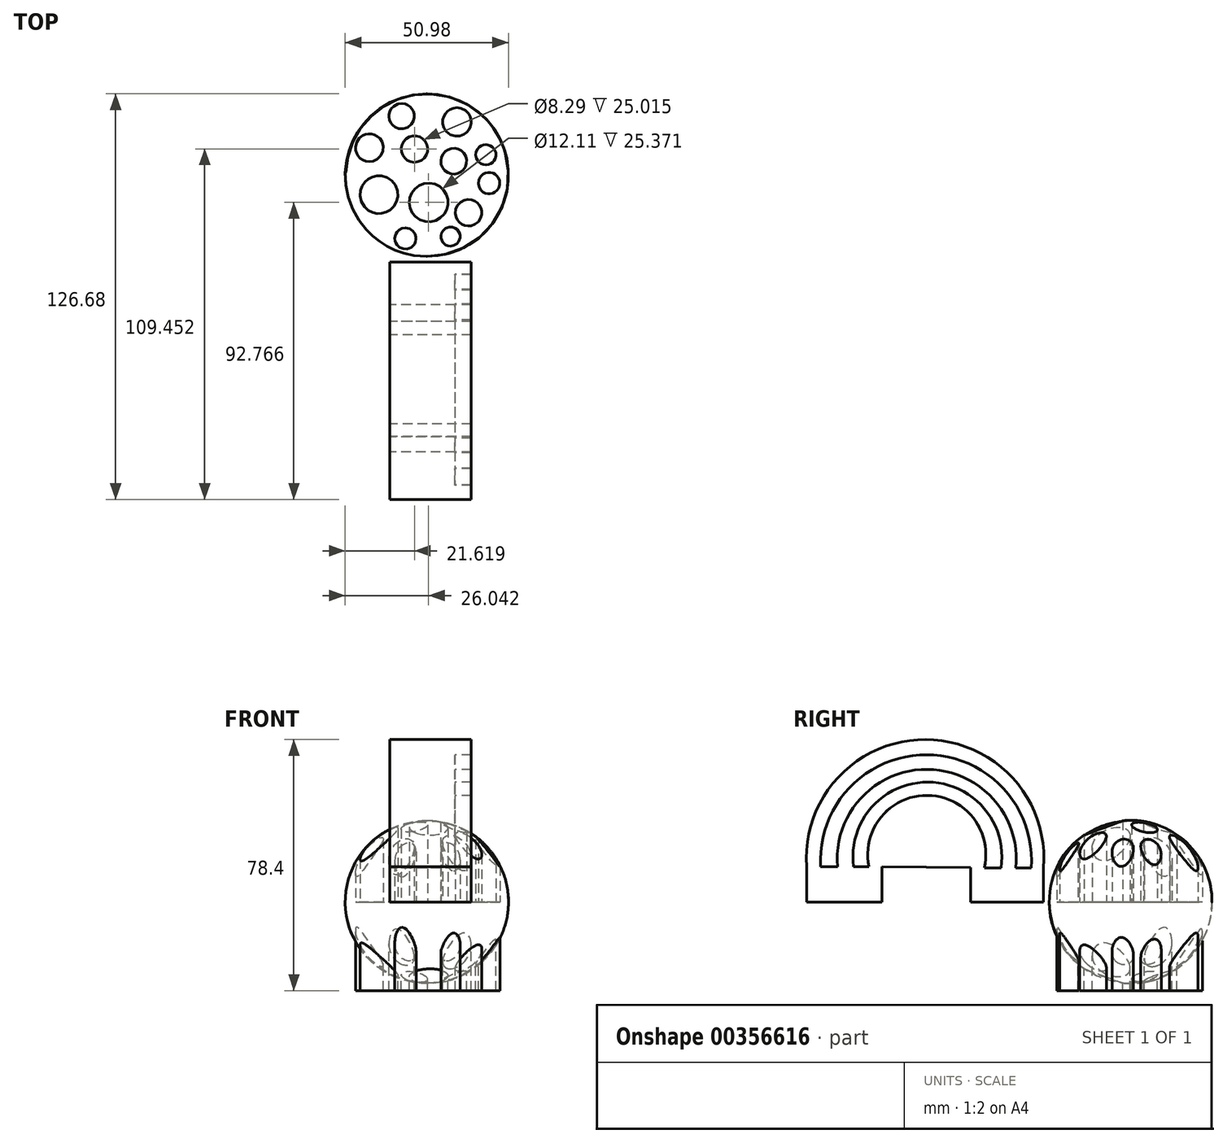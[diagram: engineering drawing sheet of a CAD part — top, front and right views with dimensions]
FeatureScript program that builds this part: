
annotation { "Feature Type Name" : "Feature", "Feature Type Description" : "" }
export const myFeature = defineFeature(function(context is Context, id is Id, definition is map)
    precondition{}
    {
        {
            var Q0;
            Q0=qCreatedBy(makeId("Top.planeOp"),FACE);
            var sketch = newSketch(context, id + "F0", { "sketchPlane" : qUnion([Q0])});
            skLineSegment(sketch, "E0", {"start": v(11.51, 50.8) * mm, "end": v(11.51, 0) * mm});
            skArc(sketch, "E1", {"start": v(11.51, 0) * mm, "mid": v(37, 25.4) * mm, "end": v(11.51, 50.8) * mm});
            skSolve(sketch);
        }
        {
            var Q0;
            Q0=makeQuery(id+"F0.imprint","IMPRINT",FACE,{"disambiguationData":[TD([[makeQuery(id+"F0.imprint","IMPRINT",EDGE,{"derivedFrom":sQuery(id+"F0.wireOp",EDGE,"E0")}),1.0]])]});
            var Q1;
            Q1=sQuery(id+"F0.wireOp",EDGE,"E0");
            revolve(context, id + "F1", {"entities" : qUnion([Q0]), "axis" : qUnion([Q1]), "revolveType" : RevolveType.FULL});
        }
        {
            var Q0;
            Q0=qCreatedBy(makeId("Top.planeOp"),FACE);
            var sketch = newSketch(context, id + "F2", { "sketchPlane" : qUnion([Q0])});
            skCircle(sketch, "E2", {"center": v(7.64, 33.57) * mm, "radius": 4.14 * mm});
            skCircle(sketch, "E3", {"center": v(20.9, 42.02) * mm, "radius": 4.45 * mm});
            skCircle(sketch, "E4", {"center": v(19.9, 29.75) * mm, "radius": 4.03 * mm});
            skCircle(sketch, "E5", {"center": v(12.06, 16.89) * mm, "radius": 6.05 * mm});
            skCircle(sketch, "E6", {"center": v(-3.42, 19.3) * mm, "radius": 5.92 * mm});
            skCircle(sketch, "E7", {"center": v(-6.43, 33.97) * mm, "radius": 4.34 * mm});
            skCircle(sketch, "E8", {"center": v(3.62, 43.82) * mm, "radius": 3.96 * mm});
            skCircle(sketch, "E9", {"center": v(30.96, 22.92) * mm, "radius": 3.35 * mm});
            skCircle(sketch, "E10", {"center": v(4.82, 5.63) * mm, "radius": 3.32 * mm});
            skCircle(sketch, "E11", {"center": v(29.95, 31.76) * mm, "radius": 3.18 * mm});
            skCircle(sketch, "E12", {"center": v(18.9, 6.23) * mm, "radius": 2.99 * mm});
            skCircle(sketch, "E13", {"center": v(24.53, 13.67) * mm, "radius": 4.14 * mm});
            skSolve(sketch);
        }
        {
            var Q0;
            Q0 = qSketchRegion(id + "F2", true);
            extrude(context, id + "F3", {"entities" : qUnion([Q0]), "operationType" : NewBodyOperationType.REMOVE, "depth" : 54.86 * mm});
        }
        {
            var Q0;
            Q0 = qSketchRegion(id + "F2", true);
            extrude(context, id + "F4", {"entities" : qUnion([Q0]), "operationType" : NewBodyOperationType.REMOVE, "oppositeDirection" : true, "depth" : 6.86 * mm});
        }
        {
            var Q0;
            Q0 = qSketchRegion(id + "F2", true);
            extrude(context, id + "F5", {"entities" : qUnion([Q0]), "operationType" : NewBodyOperationType.ADD, "oppositeDirection" : true, "depth" : 27.7 * mm});
        }
        {
            var Q0;
            Q0=qCreatedBy(makeId("Right.planeOp"),FACE);
            var sketch = newSketch(context, id + "F6", { "sketchPlane" : qUnion([Q0])});
            skLineSegment(sketch, "E14.bottom", {"start": v(-75.79, 0) * mm, "end": v(-52.27, 0) * mm});
            skLineSegment(sketch, "E14.top", {"start": v(-75.79, 11.06) * mm, "end": v(-52.27, 11.06) * mm});
            skLineSegment(sketch, "E14.left", {"start": v(-75.79, 0) * mm, "end": v(-75.79, 11.06) * mm});
            skLineSegment(sketch, "E14.right", {"start": v(-52.27, 0) * mm, "end": v(-52.27, 11.06) * mm});
            skLineSegment(sketch, "E15.bottom", {"start": v(-24.53, 0) * mm, "end": v(-1.8, 0) * mm});
            skLineSegment(sketch, "E15.top", {"start": v(-24.53, 10.65) * mm, "end": v(-1.8, 10.65) * mm});
            skLineSegment(sketch, "E15.left", {"start": v(-24.53, 0) * mm, "end": v(-24.53, 10.65) * mm});
            skLineSegment(sketch, "E15.right", {"start": v(-1.8, 0) * mm, "end": v(-1.8, 10.65) * mm});
            skArc(sketch, "E16", {"start": v(-1.8, 10.65) * mm, "mid": v(-38.58, 50.7) * mm, "end": v(-75.79, 11.06) * mm});
            skArc(sketch, "E17", {"start": v(-5.63, 10.65) * mm, "mid": v(-38.28, 45.96) * mm, "end": v(-71.37, 11.06) * mm});
            skArc(sketch, "E18", {"start": v(-10.45, 10.65) * mm, "mid": v(-38.08, 41.4) * mm, "end": v(-66.14, 11.06) * mm});
            skPoint(sketch, "E19.endSnap0", {"position": v(-64.03, 11.06) * mm});
            skLineSegment(sketch, "E20", {"start": v(-61.11, 11.06) * mm, "end": v(-15.08, 10.65) * mm});
            skArc(sketch, "E21", {"start": v(-15.08, 10.65) * mm, "mid": v(-37.86, 37.42) * mm, "end": v(-61.11, 11.06) * mm});
            skArc(sketch, "E22", {"start": v(-20.3, 10.65) * mm, "mid": v(-38.07, 33.28) * mm, "end": v(-56.29, 11.01) * mm});
            skArc(sketch, "E23", {"start": v(-24.53, 10.65) * mm, "mid": v(-38.13, 29.43) * mm, "end": v(-52.27, 11.06) * mm});
            skSolve(sketch);
        }
        {
            var Q0;
            Q0 = qSketchRegion(id + "F6", true);
            var Q1;
            {var subQ0=sQuery(id+"F6.wireOp",EDGE,"E18");Q1=makeQuery(id+"F6.imprint","IMPRINT",FACE,{"disambiguationData":[TD([[makeQuery(id+"F6.imprint","IMPRINT",EDGE,{"derivedFrom":subQ0}),1.0]])]});}
            extrude(context, id + "F7", {"entities" : qUnion([Q0, Q1]), "depth" : 25.4 * mm});
        }
        {
            var Q0;
            {var subQ0=sQuery(id+"F6.wireOp",EDGE,"E17");Q0=makeQuery(id+"F6.imprint","IMPRINT",FACE,{"disambiguationData":[TD([[makeQuery(id+"F6.imprint","IMPRINT",EDGE,{"derivedFrom":subQ0}),1.0]])]});}
            var Q1;
            {var subQ0=sQuery(id+"F6.wireOp",EDGE,"E21");Q1=makeQuery(id+"F6.imprint","IMPRINT",FACE,{"disambiguationData":[TD([[makeQuery(id+"F6.imprint","IMPRINT",EDGE,{"derivedFrom":subQ0}),1.0]])]});}
            extrude(context, id + "F8", {"entities" : qUnion([Q0, Q1]), "operationType" : NewBodyOperationType.ADD, "depth" : 20.32 * mm});
        }
    });
